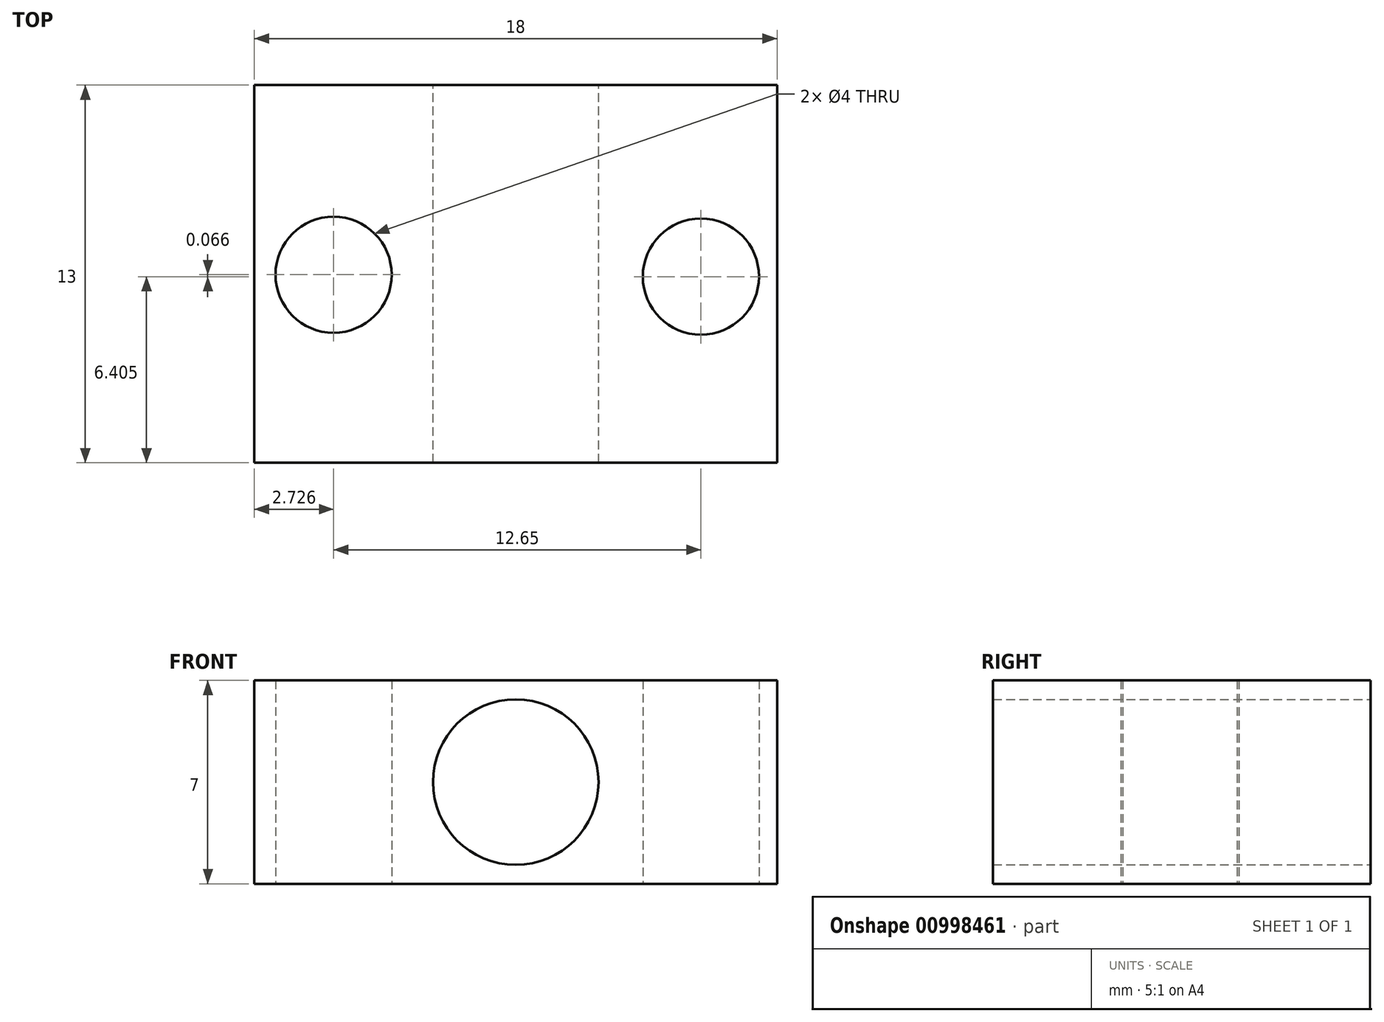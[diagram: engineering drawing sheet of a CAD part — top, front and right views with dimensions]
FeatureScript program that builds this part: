
annotation { "Feature Type Name" : "Feature", "Feature Type Description" : "" }
export const myFeature = defineFeature(function(context is Context, id is Id, definition is map)
    precondition{}
    {
        {
            var Q0;
            Q0=qCreatedBy(makeId("Front.planeOp"),FACE);
            var sketch = newSketch(context, id + "F0", { "sketchPlane" : qUnion([Q0])});
            skCircle(sketch, "E0", {"center": v(0, 0) * mm, "radius": 2.85 * mm});
            skCircle(sketch, "E1", {"center": v(0, 0) * mm, "radius": 5 * mm});
            skLineSegment(sketch, "E2.bottom", {"start": v(9, -3.5) * mm, "end": v(-9, -3.5) * mm});
            skLineSegment(sketch, "E2.top", {"start": v(9, 3.5) * mm, "end": v(-9, 3.5) * mm});
            skLineSegment(sketch, "E2.left", {"start": v(9, -3.5) * mm, "end": v(9, 3.5) * mm});
            skLineSegment(sketch, "E2.right", {"start": v(-9, -3.5) * mm, "end": v(-9, 3.5) * mm});
            skSolve(sketch);
        }
        {
            var Q0;
            {var subQ5=sQuery(id+"F0.wireOp",EDGE,"E2.left");Q0=makeQuery(id+"F0.imprint","IMPRINT",FACE,{"disambiguationData":[TD([[makeQuery(id+"F0.imprint","IMPRINT",EDGE,{"derivedFrom":subQ5}),1.0]])]});}
            var Q1;
            {var subQ5=sQuery(id+"F0.wireOp",EDGE,"E2.right");Q1=makeQuery(id+"F0.imprint","IMPRINT",FACE,{"disambiguationData":[TD([[makeQuery(id+"F0.imprint","IMPRINT",EDGE,{"derivedFrom":subQ5}),-1.0]])]});}
            var Q2;
            {var subQ0=sQuery(id+"F0.wireOp",EDGE,"E2.top");var subQ1=sQuery(id+"F0.wireOp",EDGE,"E1");var subQ2=makeQuery(id+"F0.imprint","INTERSECT",VERTEX,{"disambiguationData":[OD(0.0)],"derivedFrom":[subQ1,subQ0]});Q2=makeQuery(id+"F0.imprint","IMPRINT",FACE,{"disambiguationData":[TD([[makeQuery(id+"F0.imprint","IMPRINT",EDGE,{"disambiguationData":[TD([[subQ2,1.0]])],"derivedFrom":subQ1}),1.0]])]});}
            var Q3;
            {var subQ0=sQuery(id+"F0.wireOp",EDGE,"E2.bottom");var subQ1=sQuery(id+"F0.wireOp",EDGE,"E1");var subQ2=makeQuery(id+"F0.imprint","INTERSECT",VERTEX,{"disambiguationData":[OD(0.0)],"derivedFrom":[subQ1,subQ0]});Q3=makeQuery(id+"F0.imprint","IMPRINT",FACE,{"disambiguationData":[TD([[makeQuery(id+"F0.imprint","IMPRINT",EDGE,{"disambiguationData":[TD([[subQ2,-1.0]])],"derivedFrom":subQ1}),1.0]])]});}
            var Q4;
            {var subQ0=sQuery(id+"F0.wireOp",EDGE,"E2.bottom");var subQ1=sQuery(id+"F0.wireOp",EDGE,"E0");var subQ2=makeQuery(id+"F0.imprint","INTERSECT",VERTEX,{"derivedFrom":[subQ1,subQ0]});Q4=makeQuery(id+"F0.imprint","IMPRINT",FACE,{"disambiguationData":[TD([[makeQuery(id+"F0.imprint","IMPRINT",EDGE,{"disambiguationData":[TD([[subQ2,1.0]])],"derivedFrom":subQ1}),-1.0]])]});}
            var Q5;
            {var subQ0=sQuery(id+"F0.wireOp",EDGE,"E2.bottom");var subQ1=sQuery(id+"F0.wireOp",EDGE,"E0");var subQ2=makeQuery(id+"F0.imprint","INTERSECT",VERTEX,{"derivedFrom":[subQ1,subQ0]});Q5=makeQuery(id+"F0.imprint","IMPRINT",FACE,{"disambiguationData":[TD([[makeQuery(id+"F0.imprint","IMPRINT",EDGE,{"disambiguationData":[TD([[subQ2,-1.0]])],"derivedFrom":subQ1}),-1.0]])]});}
            extrude(context, id + "F1", {"entities" : qUnion([Q0, Q1, Q2, Q3, Q4, Q5]), "depth" : 13 * mm, "offsetDistance" : 25.4 * mm});
        }
        {
            var Q0;
            Q0=qCreatedBy(makeId("Top.planeOp"),FACE);
            var sketch = newSketch(context, id + "F2", { "sketchPlane" : qUnion([Q0])});
            skCircle(sketch, "E3", {"center": v(6.38, -6.6) * mm, "radius": 2 * mm});
            skSolve(sketch);
        }
        {
            var Q0;
            Q0 = qSketchRegion(id + "F2", true);
            extrude(context, id + "F3", {"entities" : qUnion([Q0]), "operationType" : NewBodyOperationType.REMOVE, "endBound" : BoundingType.SYMMETRIC, "depth" : 25 * mm, "offsetDistance" : 25 * mm});
        }
        {
            var Q0;
            Q0=qCreatedBy(makeId("Top.planeOp"),FACE);
            var sketch = newSketch(context, id + "F4", { "sketchPlane" : qUnion([Q0])});
            skCircle(sketch, "E4", {"center": v(-6.27, -6.53) * mm, "radius": 2 * mm});
            skSolve(sketch);
        }
        {
            var Q0;
            Q0 = qSketchRegion(id + "F4", true);
            var Q1;
            Q1=makeQuery(id+"F1.opExtrude","SWEPT_BODY",BODY,{"disambiguationData":[OSD([sQuery(id+"F0.wireOp",EDGE,"E0"),sQuery(id+"F0.wireOp",EDGE,"E1"),sQuery(id+"F0.wireOp",EDGE,"E2.bottom"),sQuery(id+"F0.wireOp",EDGE,"E2.top"),sQuery(id+"F0.wireOp",EDGE,"E2.left"),sQuery(id+"F0.wireOp",EDGE,"E2.right")])]});
            extrude(context, id + "F5", {"entities" : qUnion([Q0]), "operationType" : NewBodyOperationType.REMOVE, "endBound" : BoundingType.SYMMETRIC, "depth" : 25 * mm, "endBoundEntityBody" : qUnion([Q1]), "offsetDistance" : 25 * mm});
        }
    });
